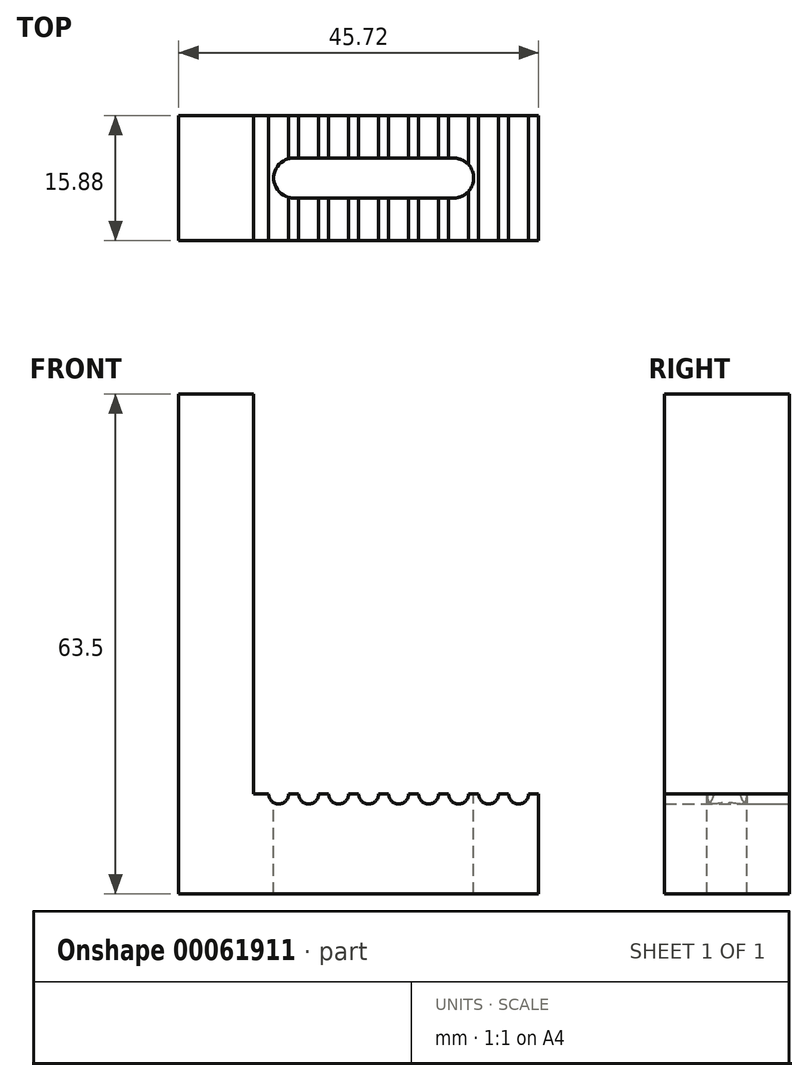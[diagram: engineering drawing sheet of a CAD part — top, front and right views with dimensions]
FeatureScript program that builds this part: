
annotation { "Feature Type Name" : "Feature", "Feature Type Description" : "" }
export const myFeature = defineFeature(function(context is Context, id is Id, definition is map)
    precondition{}
    {
        {
            var Q0;
            Q0=qCreatedBy(makeId("Front.planeOp"),FACE);
            var sketch = newSketch(context, id + "F0", { "sketchPlane" : qUnion([Q0])});
            skLineSegment(sketch, "E0", {"start": v(0, 0) * mm, "end": v(-45.72, 0) * mm});
            skLineSegment(sketch, "E1", {"start": v(-45.72, 0) * mm, "end": v(-45.72, 63.5) * mm});
            skLineSegment(sketch, "E2", {"start": v(-45.72, 63.5) * mm, "end": v(-36.2, 63.5) * mm});
            skLineSegment(sketch, "E3", {"start": v(-36.2, 63.5) * mm, "end": v(-36.2, 12.7) * mm});
            skLineSegment(sketch, "E4", {"start": v(-36.2, 12.7) * mm, "end": v(0, 12.7) * mm});
            skLineSegment(sketch, "E5", {"start": v(0, 12.7) * mm, "end": v(0, 0) * mm});
            skSolve(sketch);
        }
        {
            var Q0;
            Q0=makeQuery(id+"F0.imprint","IMPRINT",FACE,{"disambiguationData":[TD([[makeQuery(id+"F0.imprint","IMPRINT",EDGE,{"derivedFrom":sQuery(id+"F0.wireOp",EDGE,"E0")}),-1.0]])]});
            extrude(context, id + "F1", {"entities" : qUnion([Q0]), "depth" : 15.88 * mm});
        }
        {
            var Q0;
            Q0=makeQuery(id+"F1.opExtrude","SWEPT_FACE",FACE,{"disambiguationData":[OSD([sQuery(id+"F0.wireOp",EDGE,"E4")])]});
            var sketch = newSketch(context, id + "F2", { "sketchPlane" : qUnion([Q0])});
            skLineSegment(sketch, "E6", {"start": v(-36.2, -7.94) * mm, "end": v(0, -7.94) * mm, "construction": true});
            skLineSegment(sketch, "E7", {"start": v(-18.1, 0) * mm, "end": v(-18.1, -15.88) * mm, "construction": true});
            skArc(sketch, "E8", {"start": v(-31.12, -5.4) * mm, "mid": v(-33.66, -7.94) * mm, "end": v(-31.12, -10.48) * mm});
            skArc(sketch, "E9", {"start": v(-10.8, -10.48) * mm, "mid": v(-8.25, -7.94) * mm, "end": v(-10.8, -5.4) * mm});
            skLineSegment(sketch, "E10", {"start": v(-31.12, -5.4) * mm, "end": v(-10.8, -5.4) * mm});
            skLineSegment(sketch, "E11", {"start": v(-10.8, -10.48) * mm, "end": v(-31.12, -10.48) * mm});
            skSolve(sketch);
        }
        {
            var Q0;
            Q0=makeQuery(id+"F2.imprint","IMPRINT",FACE,{"disambiguationData":[TD([[makeQuery(id+"F2.imprint","IMPRINT",EDGE,{"derivedFrom":sQuery(id+"F2.wireOp",EDGE,"E8")}),1.0]])]});
            extrude(context, id + "F3", {"entities" : qUnion([Q0]), "operationType" : NewBodyOperationType.REMOVE, "oppositeDirection" : true, "depth" : 25.4 * mm});
        }
        {
            var Q0;
            Q0=makeQuery(id+"F1.opExtrude","CAP_FACE",FACE,{"disambiguationData":[OSD([sQuery(id+"F0.wireOp",EDGE,"E0"),sQuery(id+"F0.wireOp",EDGE,"E1"),sQuery(id+"F0.wireOp",EDGE,"E2"),sQuery(id+"F0.wireOp",EDGE,"E3"),sQuery(id+"F0.wireOp",EDGE,"E4"),sQuery(id+"F0.wireOp",EDGE,"E5")])],"isStart":true});
            var sketch = newSketch(context, id + "F4", { "sketchPlane" : qUnion([Q0])});
            skCircle(sketch, "E12", {"center": v(25.4, 12.7) * mm, "radius": 1.27 * mm});
            skCircle(sketch, "E13", {"center": v(21.59, 12.7) * mm, "radius": 1.27 * mm});
            skCircle(sketch, "E14", {"center": v(17.78, 12.7) * mm, "radius": 1.27 * mm});
            skCircle(sketch, "E15", {"center": v(13.97, 12.7) * mm, "radius": 1.27 * mm});
            skCircle(sketch, "E16", {"center": v(10.16, 12.7) * mm, "radius": 1.27 * mm});
            skCircle(sketch, "E17", {"center": v(6.35, 12.7) * mm, "radius": 1.27 * mm});
            skCircle(sketch, "E18", {"center": v(2.54, 12.7) * mm, "radius": 1.27 * mm});
            skCircle(sketch, "E19", {"center": v(29.21, 12.7) * mm, "radius": 1.27 * mm});
            skCircle(sketch, "E20", {"center": v(33.02, 12.7) * mm, "radius": 1.27 * mm});
            skSolve(sketch);
        }
        {
            var Q0;
            {var subQ0=sQuery(id+"F4.wireOp",EDGE,"E12");var subQ1=makeQuery(id+"F1.opExtrude","CAP_EDGE",EDGE,{"disambiguationData":[OSD([sQuery(id+"F0.wireOp",EDGE,"E4")])],"isStart":true});var subQ2=makeQuery(id+"F4.imprint","INTERSECT",VERTEX,{"disambiguationData":[OD(0.0)],"derivedFrom":[subQ1,subQ0]});Q0=makeQuery(id+"F4.imprint","IMPRINT",FACE,{"disambiguationData":[TD([[makeQuery(id+"F4.imprint","IMPRINT",EDGE,{"disambiguationData":[TD([[subQ2,1.0]])],"derivedFrom":subQ0}),1.0]])]});}
            var Q1;
            {var subQ0=sQuery(id+"F4.wireOp",EDGE,"E13");var subQ1=makeQuery(id+"F1.opExtrude","CAP_EDGE",EDGE,{"disambiguationData":[OSD([sQuery(id+"F0.wireOp",EDGE,"E4")])],"isStart":true});var subQ2=makeQuery(id+"F4.imprint","INTERSECT",VERTEX,{"disambiguationData":[OD(0.0)],"derivedFrom":[subQ1,subQ0]});Q1=makeQuery(id+"F4.imprint","IMPRINT",FACE,{"disambiguationData":[TD([[makeQuery(id+"F4.imprint","IMPRINT",EDGE,{"disambiguationData":[TD([[subQ2,1.0]])],"derivedFrom":subQ0}),1.0]])]});}
            var Q2;
            {var subQ0=sQuery(id+"F4.wireOp",EDGE,"E14");var subQ1=makeQuery(id+"F1.opExtrude","CAP_EDGE",EDGE,{"disambiguationData":[OSD([sQuery(id+"F0.wireOp",EDGE,"E4")])],"isStart":true});var subQ2=makeQuery(id+"F4.imprint","INTERSECT",VERTEX,{"disambiguationData":[OD(0.0)],"derivedFrom":[subQ1,subQ0]});Q2=makeQuery(id+"F4.imprint","IMPRINT",FACE,{"disambiguationData":[TD([[makeQuery(id+"F4.imprint","IMPRINT",EDGE,{"disambiguationData":[TD([[subQ2,1.0]])],"derivedFrom":subQ0}),1.0]])]});}
            var Q3;
            {var subQ0=sQuery(id+"F4.wireOp",EDGE,"E15");var subQ1=makeQuery(id+"F1.opExtrude","CAP_EDGE",EDGE,{"disambiguationData":[OSD([sQuery(id+"F0.wireOp",EDGE,"E4")])],"isStart":true});var subQ2=makeQuery(id+"F4.imprint","INTERSECT",VERTEX,{"disambiguationData":[OD(0.0)],"derivedFrom":[subQ1,subQ0]});Q3=makeQuery(id+"F4.imprint","IMPRINT",FACE,{"disambiguationData":[TD([[makeQuery(id+"F4.imprint","IMPRINT",EDGE,{"disambiguationData":[TD([[subQ2,-1.0]])],"derivedFrom":subQ0}),1.0]])]});}
            var Q4;
            {var subQ0=sQuery(id+"F4.wireOp",EDGE,"E16");var subQ1=makeQuery(id+"F1.opExtrude","CAP_EDGE",EDGE,{"disambiguationData":[OSD([sQuery(id+"F0.wireOp",EDGE,"E4")])],"isStart":true});var subQ2=makeQuery(id+"F4.imprint","INTERSECT",VERTEX,{"disambiguationData":[OD(0.0)],"derivedFrom":[subQ1,subQ0]});Q4=makeQuery(id+"F4.imprint","IMPRINT",FACE,{"disambiguationData":[TD([[makeQuery(id+"F4.imprint","IMPRINT",EDGE,{"disambiguationData":[TD([[subQ2,-1.0]])],"derivedFrom":subQ0}),1.0]])]});}
            var Q5;
            {var subQ0=sQuery(id+"F4.wireOp",EDGE,"E17");var subQ1=makeQuery(id+"F1.opExtrude","CAP_EDGE",EDGE,{"disambiguationData":[OSD([sQuery(id+"F0.wireOp",EDGE,"E4")])],"isStart":true});var subQ2=makeQuery(id+"F4.imprint","INTERSECT",VERTEX,{"disambiguationData":[OD(0.0)],"derivedFrom":[subQ1,subQ0]});Q5=makeQuery(id+"F4.imprint","IMPRINT",FACE,{"disambiguationData":[TD([[makeQuery(id+"F4.imprint","IMPRINT",EDGE,{"disambiguationData":[TD([[subQ2,-1.0]])],"derivedFrom":subQ0}),1.0]])]});}
            var Q6;
            {var subQ0=sQuery(id+"F4.wireOp",EDGE,"E18");var subQ1=makeQuery(id+"F1.opExtrude","CAP_EDGE",EDGE,{"disambiguationData":[OSD([sQuery(id+"F0.wireOp",EDGE,"E4")])],"isStart":true});var subQ2=makeQuery(id+"F4.imprint","INTERSECT",VERTEX,{"disambiguationData":[OD(0.0)],"derivedFrom":[subQ1,subQ0]});Q6=makeQuery(id+"F4.imprint","IMPRINT",FACE,{"disambiguationData":[TD([[makeQuery(id+"F4.imprint","IMPRINT",EDGE,{"disambiguationData":[TD([[subQ2,-1.0]])],"derivedFrom":subQ0}),1.0]])]});}
            var Q7;
            {var subQ0=sQuery(id+"F4.wireOp",EDGE,"E19");var subQ1=makeQuery(id+"F1.opExtrude","CAP_EDGE",EDGE,{"disambiguationData":[OSD([sQuery(id+"F0.wireOp",EDGE,"E4")])],"isStart":true});var subQ2=makeQuery(id+"F4.imprint","INTERSECT",VERTEX,{"disambiguationData":[OD(0.0)],"derivedFrom":[subQ1,subQ0]});Q7=makeQuery(id+"F4.imprint","IMPRINT",FACE,{"disambiguationData":[TD([[makeQuery(id+"F4.imprint","IMPRINT",EDGE,{"disambiguationData":[TD([[subQ2,1.0]])],"derivedFrom":subQ0}),1.0]])]});}
            var Q8;
            {var subQ0=sQuery(id+"F4.wireOp",EDGE,"E20");var subQ1=makeQuery(id+"F1.opExtrude","CAP_EDGE",EDGE,{"disambiguationData":[OSD([sQuery(id+"F0.wireOp",EDGE,"E4")])],"isStart":true});var subQ2=makeQuery(id+"F4.imprint","INTERSECT",VERTEX,{"disambiguationData":[OD(0.0)],"derivedFrom":[subQ1,subQ0]});Q8=makeQuery(id+"F4.imprint","IMPRINT",FACE,{"disambiguationData":[TD([[makeQuery(id+"F4.imprint","IMPRINT",EDGE,{"disambiguationData":[TD([[subQ2,1.0]])],"derivedFrom":subQ0}),1.0]])]});}
            extrude(context, id + "F5", {"entities" : qUnion([Q0, Q1, Q2, Q3, Q4, Q5, Q6, Q7, Q8]), "operationType" : NewBodyOperationType.REMOVE, "oppositeDirection" : true, "depth" : 25.4 * mm});
        }
    });
